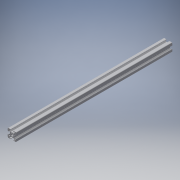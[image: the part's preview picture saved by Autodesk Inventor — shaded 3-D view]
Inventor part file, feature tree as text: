
AUTODESK INVENTOR PART (.ipt)
format: ipt  version: 2016 (Build 200138000, 138)  size: 314,880 bytes
history: native  units: in
note: dims shown in document units (in); Inventor stores cm internally (conversion verified against a paired STEP export)
features: other x3, extrude x1, sketch x1
ambient origin geometry x8: Origin, YZ Plane, XZ Plane, XY Plane, X Axis, Y Axis, Z Axis, Center Point
bodies: Solid1 (feature_tree)
feature tree (5):
  other  "Blocks"
  extrude  "Extrusion1"  [1 undecoded]
  sketch  "Sketch1"  dims[d1=0.0in]
  other  "20x20"
  other  "20x20:1"
note: 1 required parameter value undecoded (feature->parameter linkage not recoverable at this tier; creation-order binding heuristic only, values carry confidence <= 0.55)
